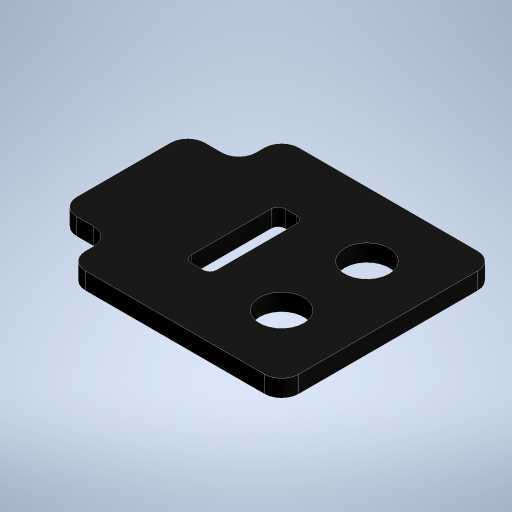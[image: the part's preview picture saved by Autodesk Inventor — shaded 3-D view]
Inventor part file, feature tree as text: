
AUTODESK INVENTOR PART (.ipt)
format: ipt  version: 2024.2 (Build 282272000, 272)  size: 271,360 bytes
history: native  units: mm
features: fillet x2, other x1, extrude x1, sketch x1
ambient origin geometry x8: Origin, YZ Plane, XZ Plane, XY Plane, X Axis, Y Axis, Z Axis, Center Point
bodies: Body1 (feature_tree)
feature tree (5):
  other  "Bryła1"
  extrude  "Wyciągnięcie proste1"  Depth=5.2mm
  fillet  "Zaokrąglenie1"  Radius=25.0mm
  fillet  "Zaokrąglenie2"  Radius=25.0mm
  sketch  "Szkic1"
